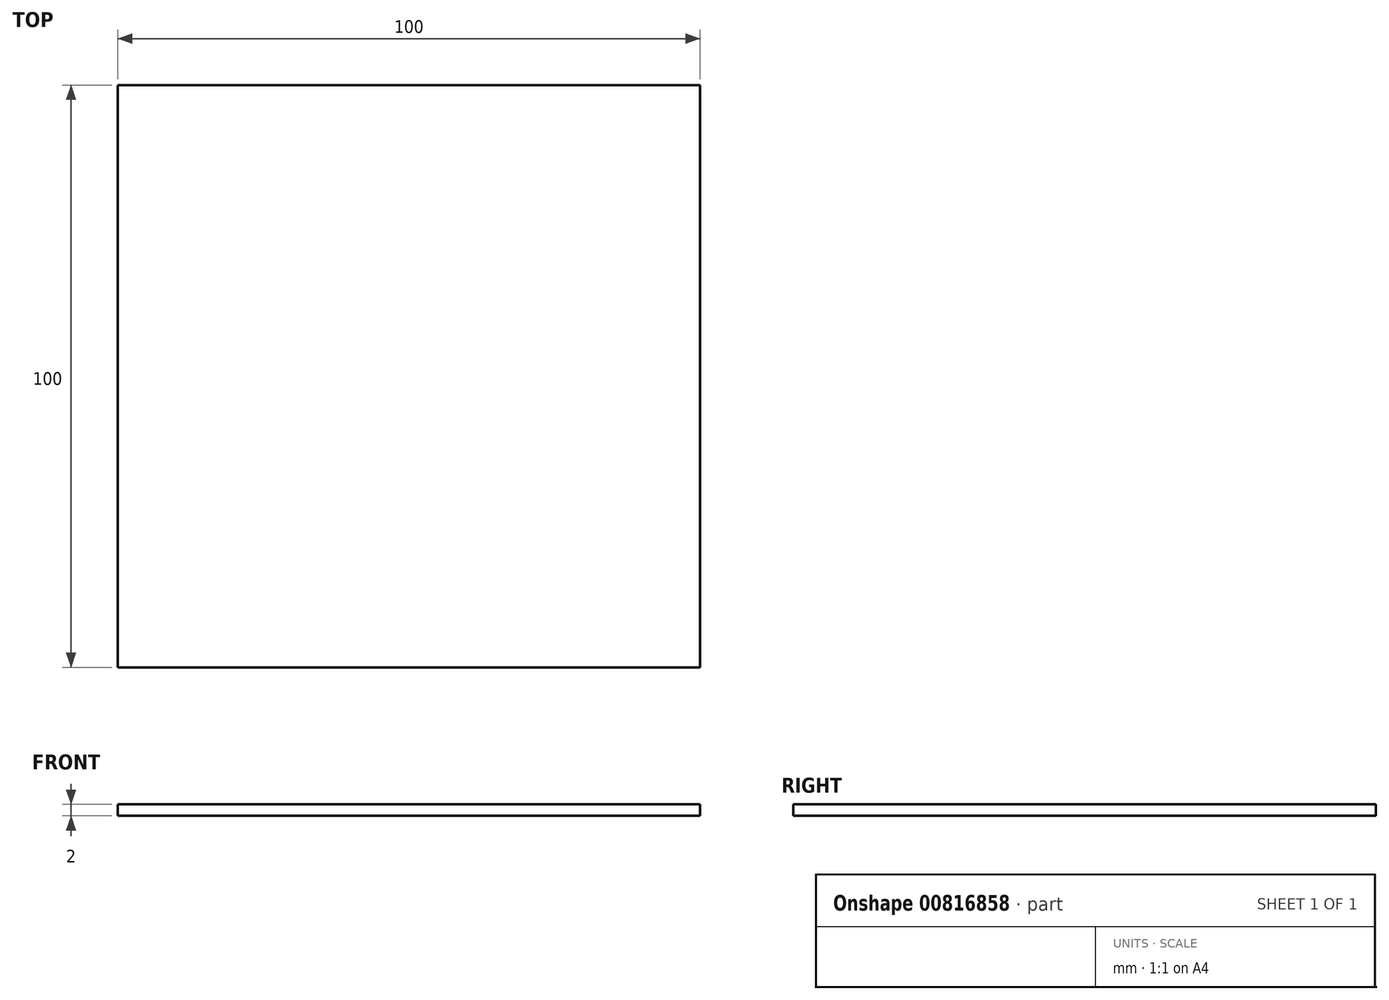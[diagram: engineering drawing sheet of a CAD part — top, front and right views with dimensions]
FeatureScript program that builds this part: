
annotation { "Feature Type Name" : "Feature", "Feature Type Description" : "" }
export const myFeature = defineFeature(function(context is Context, id is Id, definition is map)
    precondition{}
    {
        {
            var Q0;
            Q0=qCreatedBy(makeId("Front.planeOp"),FACE);
            var sketch = newSketch(context, id + "F0", { "sketchPlane" : qUnion([Q0])});
            skLineSegment(sketch, "E0.bottom", {"start": v(-51.14, 2) * mm, "end": v(48.86, 2) * mm});
            skLineSegment(sketch, "E0.top", {"start": v(-51.14, 0) * mm, "end": v(48.86, 0) * mm});
            skLineSegment(sketch, "E0.left", {"start": v(-51.14, 2) * mm, "end": v(-51.14, 0) * mm});
            skLineSegment(sketch, "E0.right", {"start": v(48.86, 2) * mm, "end": v(48.86, 0) * mm});
            skSolve(sketch);
        }
        {
            var Q0;
            Q0 = qSketchRegion(id + "F0", true);
            extrude(context, id + "F1", {"entities" : qUnion([Q0]), "depth" : 100 * mm, "offsetDistance" : 25 * mm});
        }
    });
